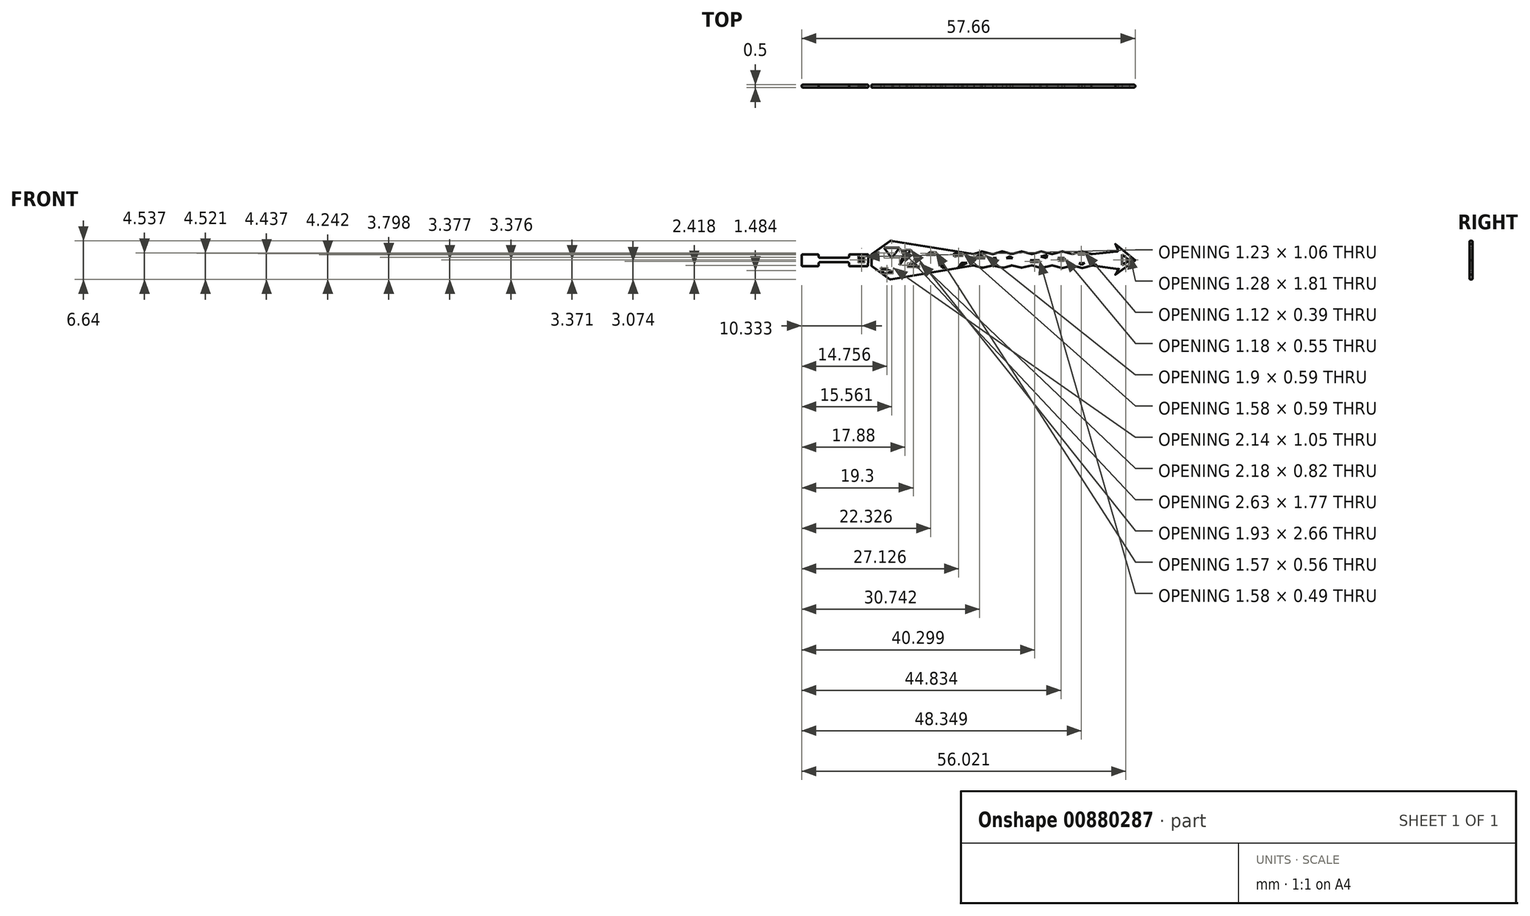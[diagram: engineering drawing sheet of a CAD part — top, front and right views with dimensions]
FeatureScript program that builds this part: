
annotation { "Feature Type Name" : "Feature", "Feature Type Description" : "" }
export const myFeature = defineFeature(function(context is Context, id is Id, definition is map)
    precondition{}
    {
        {
            var Q0;
            Q0=qCreatedBy(makeId("Front.planeOp"),FACE);
            var sketch = newSketch(context, id + "F0", { "sketchPlane" : qUnion([Q0])});
            skLineSegment(sketch, "E0", {"start": v(14.04, 0) * mm, "end": v(10.62, 2.77) * mm});
            skLineSegment(sketch, "E1", {"start": v(10.62, 2.77) * mm, "end": v(11.16, 1.51) * mm});
            skLineSegment(sketch, "E2", {"start": v(11.16, 1.51) * mm, "end": v(6.56, 1.02) * mm});
            skLineSegment(sketch, "E3", {"start": v(6.56, 1.02) * mm, "end": v(4.86, 1.51) * mm});
            skLineSegment(sketch, "E4", {"start": v(4.86, 1.51) * mm, "end": v(3.19, 1.02) * mm});
            skLineSegment(sketch, "E5", {"start": v(3.19, 1.02) * mm, "end": v(1.45, 1.51) * mm});
            skLineSegment(sketch, "E6", {"start": v(1.45, 1.51) * mm, "end": v(-0.33, 1.02) * mm});
            skLineSegment(sketch, "E7", {"start": v(-0.33, 1.02) * mm, "end": v(-2.2, 1.51) * mm});
            skLineSegment(sketch, "E8", {"start": v(-2.2, 1.51) * mm, "end": v(-3.84, 1.02) * mm});
            skLineSegment(sketch, "E9", {"start": v(-3.84, 1.02) * mm, "end": v(-5.58, 1.51) * mm});
            skLineSegment(sketch, "E10", {"start": v(-5.58, 1.51) * mm, "end": v(-7.29, 1.02) * mm});
            skLineSegment(sketch, "E11", {"start": v(-7.29, 1.02) * mm, "end": v(-8.89, 1.51) * mm});
            skLineSegment(sketch, "E12", {"start": v(-8.89, 1.51) * mm, "end": v(-10.66, 1.02) * mm});
            skLineSegment(sketch, "E13", {"start": v(-10.66, 1.02) * mm, "end": v(-12.44, 1.51) * mm});
            skLineSegment(sketch, "E14", {"start": v(-12.44, 1.51) * mm, "end": v(-13.9, 1.02) * mm});
            skLineSegment(sketch, "E15", {"start": v(-13.9, 1.02) * mm, "end": v(-28.31, 3.32) * mm});
            skLineSegment(sketch, "E16", {"start": v(-28.31, 3.32) * mm, "end": v(-31.55, 1.02) * mm});
            skLineSegment(sketch, "E17", {"start": v(-31.55, 1.02) * mm, "end": v(-31.55, -1) * mm});
            skLineSegment(sketch, "E18", {"start": v(-31.55, -1) * mm, "end": v(-28.31, -3.33) * mm});
            skLineSegment(sketch, "E19", {"start": v(-28.31, -3.33) * mm, "end": v(-13.9, -0.92) * mm});
            skLineSegment(sketch, "E20", {"start": v(-13.9, -0.92) * mm, "end": v(-12.44, -1.33) * mm});
            skLineSegment(sketch, "E21", {"start": v(-12.44, -1.33) * mm, "end": v(-10.66, -0.92) * mm});
            skLineSegment(sketch, "E22", {"start": v(-10.66, -0.92) * mm, "end": v(-8.89, -1.33) * mm});
            skLineSegment(sketch, "E23", {"start": v(-8.89, -1.33) * mm, "end": v(-7.29, -0.92) * mm});
            skLineSegment(sketch, "E24", {"start": v(-7.29, -0.92) * mm, "end": v(-5.58, -1.33) * mm});
            skLineSegment(sketch, "E25", {"start": v(-5.58, -1.33) * mm, "end": v(-3.84, -0.92) * mm});
            skLineSegment(sketch, "E26", {"start": v(-3.84, -0.92) * mm, "end": v(-2.2, -1.35) * mm});
            skLineSegment(sketch, "E27", {"start": v(-2.2, -1.35) * mm, "end": v(-0.33, -0.92) * mm});
            skLineSegment(sketch, "E28", {"start": v(-0.33, -0.92) * mm, "end": v(1.45, -1.35) * mm});
            skLineSegment(sketch, "E29", {"start": v(1.45, -1.35) * mm, "end": v(3.19, -0.92) * mm});
            skLineSegment(sketch, "E30", {"start": v(3.19, -0.92) * mm, "end": v(4.86, -1.35) * mm});
            skLineSegment(sketch, "E31", {"start": v(4.86, -1.35) * mm, "end": v(6.56, -0.92) * mm});
            skLineSegment(sketch, "E32", {"start": v(6.56, -0.92) * mm, "end": v(11.16, -1.53) * mm});
            skLineSegment(sketch, "E33", {"start": v(11.16, -1.53) * mm, "end": v(10.62, -2.51) * mm});
            skLineSegment(sketch, "E34", {"start": v(10.62, -2.51) * mm, "end": v(14.04, 0) * mm});
            skSolve(sketch);
        }
        {
            var Q0;
            Q0 = qSketchRegion(id + "F0", true);
            extrude(context, id + "F1", {"entities" : qUnion([Q0]), "depth" : .25 * mm, "offsetDistance" : 25 * mm, "hasSecondDirection" : true, "secondDirectionOppositeDirection" : true, "secondDirectionDepth" : .25 * mm});
        }
        {
            var Q0;
            Q0=qCreatedBy(makeId("Front.planeOp"),FACE);
            var sketch = newSketch(context, id + "F2", { "sketchPlane" : qUnion([Q0])});
            skLineSegment(sketch, "E35", {"start": v(13.04, 0) * mm, "end": v(11.76, 0.95) * mm});
            skLineSegment(sketch, "E36", {"start": v(11.76, 0.95) * mm, "end": v(11.76, -0.85) * mm});
            skLineSegment(sketch, "E37", {"start": v(11.76, -0.85) * mm, "end": v(13.04, 0) * mm});
            skLineSegment(sketch, "E38", {"start": v(5.29, -0.5) * mm, "end": v(4.76, -0.85) * mm});
            skLineSegment(sketch, "E39", {"start": v(4.76, -0.85) * mm, "end": v(4.36, -0.55) * mm});
            skLineSegment(sketch, "E40", {"start": v(4.36, -0.55) * mm, "end": v(5.29, -0.5) * mm});
            skLineSegment(sketch, "E41", {"start": v(5.29, 0.92) * mm, "end": v(4.76, 1.31) * mm});
            skLineSegment(sketch, "E42", {"start": v(4.76, 1.31) * mm, "end": v(4.17, 0.95) * mm});
            skLineSegment(sketch, "E43", {"start": v(4.17, 0.95) * mm, "end": v(5.29, 0.92) * mm});
            skLineSegment(sketch, "E44", {"start": v(1.8, 0.33) * mm, "end": v(0.62, 0.33) * mm});
            skLineSegment(sketch, "E45", {"start": v(0.62, 0.33) * mm, "end": v(1.36, -0.22) * mm});
            skLineSegment(sketch, "E46", {"start": v(1.36, -0.22) * mm, "end": v(1.8, 0.33) * mm});
            skLineSegment(sketch, "E47", {"start": v(-1.18, 0.92) * mm, "end": v(-2.27, 0.6) * mm});
            skLineSegment(sketch, "E48", {"start": v(-2.27, 0.6) * mm, "end": v(-1.35, 0.33) * mm});
            skLineSegment(sketch, "E49", {"start": v(-1.35, 0.33) * mm, "end": v(-1.18, 0.92) * mm});
            skLineSegment(sketch, "E50", {"start": v(-2.53, 0) * mm, "end": v(-3.45, -0.5) * mm});
            skLineSegment(sketch, "E51", {"start": v(-3.45, -0.5) * mm, "end": v(-4.11, 0) * mm});
            skLineSegment(sketch, "E52", {"start": v(-4.11, 0) * mm, "end": v(-2.53, 0) * mm});
            skLineSegment(sketch, "E53", {"start": v(-8.25, 0.33) * mm, "end": v(-7.63, 0.66) * mm});
            skLineSegment(sketch, "E54", {"start": v(-7.63, 0.66) * mm, "end": v(-7.18, 0.33) * mm});
            skLineSegment(sketch, "E55", {"start": v(-7.18, 0.33) * mm, "end": v(-8.25, 0.33) * mm});
            skLineSegment(sketch, "E56", {"start": v(-10.55, -0.5) * mm, "end": v(-9.94, 0.33) * mm});
            skLineSegment(sketch, "E57", {"start": v(-9.94, 0.33) * mm, "end": v(-10.51, 0.33) * mm});
            skLineSegment(sketch, "E58", {"start": v(-10.51, 0.33) * mm, "end": v(-10.55, -0.5) * mm});
            skLineSegment(sketch, "E59", {"start": v(-11.93, 0.33) * mm, "end": v(-12.72, 0.92) * mm});
            skLineSegment(sketch, "E60", {"start": v(-12.72, 0.92) * mm, "end": v(-13.83, 0.33) * mm});
            skLineSegment(sketch, "E61", {"start": v(-13.83, 0.33) * mm, "end": v(-11.93, 0.33) * mm});
            skLineSegment(sketch, "E62", {"start": v(-15.05, -0.5) * mm, "end": v(-16.63, -1.33) * mm});
            skLineSegment(sketch, "E63", {"start": v(-16.63, -1.33) * mm, "end": v(-16, -0.5) * mm});
            skLineSegment(sketch, "E64", {"start": v(-16, -0.5) * mm, "end": v(-15.05, -0.5) * mm});
            skLineSegment(sketch, "E65", {"start": v(-17.28, 0.63) * mm, "end": v(-15.7, 0.92) * mm});
            skLineSegment(sketch, "E66", {"start": v(-15.7, 0.92) * mm, "end": v(-17.28, 1.22) * mm});
            skLineSegment(sketch, "E67", {"start": v(-17.28, 1.22) * mm, "end": v(-17.28, 0.63) * mm});
            skLineSegment(sketch, "E68", {"start": v(-18.8, -1.31) * mm, "end": v(-19.68, -0.65) * mm});
            skLineSegment(sketch, "E69", {"start": v(-19.68, -0.65) * mm, "end": v(-19.33, -1.31) * mm});
            skLineSegment(sketch, "E70", {"start": v(-19.33, -1.31) * mm, "end": v(-18.8, -1.31) * mm});
            skLineSegment(sketch, "E71", {"start": v(-21.26, 1.48) * mm, "end": v(-20.5, 0.92) * mm});
            skLineSegment(sketch, "E72", {"start": v(-20.5, 0.92) * mm, "end": v(-22.08, 0.92) * mm});
            skLineSegment(sketch, "E73", {"start": v(-22.08, 0.92) * mm, "end": v(-21.26, 1.48) * mm});
            skLineSegment(sketch, "E74", {"start": v(-23.23, -1.31) * mm, "end": v(-24.33, -0.5) * mm});
            skLineSegment(sketch, "E75", {"start": v(-24.33, -0.5) * mm, "end": v(-25.41, -1.07) * mm});
            skLineSegment(sketch, "E76", {"start": v(-25.41, -1.07) * mm, "end": v(-23.23, -1.31) * mm});
            skLineSegment(sketch, "E77", {"start": v(-29.37, 2.1) * mm, "end": v(-26.74, 2.1) * mm});
            skLineSegment(sketch, "E78", {"start": v(-26.74, 2.1) * mm, "end": v(-28.07, 0.33) * mm});
            skLineSegment(sketch, "E79", {"start": v(-28.07, 0.33) * mm, "end": v(-29.37, 2.1) * mm});
            skLineSegment(sketch, "E80", {"start": v(-24.77, 1.74) * mm, "end": v(-26.7, -0.85) * mm});
            skLineSegment(sketch, "E81", {"start": v(-26.7, -0.85) * mm, "end": v(-25.56, 1.8) * mm});
            skLineSegment(sketch, "E82", {"start": v(-25.56, 1.8) * mm, "end": v(-24.77, 1.74) * mm});
            skLineSegment(sketch, "E83", {"start": v(-27.8, -1.97) * mm, "end": v(-29.93, -1.31) * mm});
            skLineSegment(sketch, "E84", {"start": v(-29.93, -1.31) * mm, "end": v(-29.37, -2.36) * mm});
            skLineSegment(sketch, "E85", {"start": v(-29.37, -2.36) * mm, "end": v(-27.8, -1.97) * mm});
            skSolve(sketch);
        }
        {
            var Q0;
            Q0 = qSketchRegion(id + "F2", true);
            extrude(context, id + "F3", {"entities" : qUnion([Q0]), "operationType" : NewBodyOperationType.REMOVE, "oppositeDirection" : true, "depth" : 25 * mm, "offsetDistance" : 25 * mm, "hasSecondDirection" : true, "secondDirectionOppositeDirection" : false, "secondDirectionDepth" : 25 * mm});
        }
        {
            var Q0;
            Q0=makeQuery(id+"F1.opExtrude","CAP_EDGE",EDGE,{"disambiguationData":[OSD([sQuery(id+"F0.wireOp",EDGE,"E0")])],"isStart":true});
            var Q1;
            Q1=makeQuery(id+"F1.opExtrude","CAP_EDGE",EDGE,{"disambiguationData":[OSD([sQuery(id+"F0.wireOp",EDGE,"E0")])],"isStart":false});
            var Q2;
            Q2=makeQuery(id+"F1.opExtrude","CAP_EDGE",EDGE,{"disambiguationData":[OSD([sQuery(id+"F0.wireOp",EDGE,"E34")])],"isStart":true});
            var Q3;
            Q3=makeQuery(id+"F1.opExtrude","CAP_EDGE",EDGE,{"disambiguationData":[OSD([sQuery(id+"F0.wireOp",EDGE,"E34")])],"isStart":false});
            fillet(context, id + "F4", {"entities" : qUnion([Q0, Q1, Q2, Q3]), "radius" : .2 * mm, "tangentPropagation" : true, "allowEdgeOverflow" : false});
        }
        {
            var Q0;
            Q0=makeQuery(id+"F1.opExtrude","SWEPT_FACE",FACE,{"disambiguationData":[OSD([sQuery(id+"F0.wireOp",EDGE,"E2")])]});
            fillet(context, id + "F5", {"entities" : qUnion([Q0]), "radius" : .2 * mm, "tangentPropagation" : true, "allowEdgeOverflow" : false});
        }
        {
            var Q0;
            Q0=makeQuery(id+"F1.opExtrude","CAP_EDGE",EDGE,{"disambiguationData":[OSD([sQuery(id+"F0.wireOp",EDGE,"E32")])],"isStart":true});
            var Q1;
            Q1=makeQuery(id+"F1.opExtrude","CAP_EDGE",EDGE,{"disambiguationData":[OSD([sQuery(id+"F0.wireOp",EDGE,"E32")])],"isStart":false});
            fillet(context, id + "F6", {"entities" : qUnion([Q0, Q1]), "radius" : .2 * mm, "tangentPropagation" : true, "allowEdgeOverflow" : false});
        }
        {
            var Q0;
            Q0=makeQuery(id+"F1.opExtrude","CAP_EDGE",EDGE,{"disambiguationData":[OSD([sQuery(id+"F0.wireOp",EDGE,"E31")])],"isStart":false});
            var Q1;
            Q1=makeQuery(id+"F1.opExtrude","CAP_EDGE",EDGE,{"disambiguationData":[OSD([sQuery(id+"F0.wireOp",EDGE,"E30")])],"isStart":false});
            var Q2;
            Q2=makeQuery(id+"F1.opExtrude","SWEPT_FACE",FACE,{"disambiguationData":[OSD([sQuery(id+"F0.wireOp",EDGE,"E31")])]});
            var Q3;
            Q3=makeQuery(id+"F1.opExtrude","SWEPT_FACE",FACE,{"disambiguationData":[OSD([sQuery(id+"F0.wireOp",EDGE,"E30")])]});
            var Q4;
            Q4=makeQuery(id+"F1.opExtrude","SWEPT_FACE",FACE,{"disambiguationData":[OSD([sQuery(id+"F0.wireOp",EDGE,"E29")])]});
            var Q5;
            Q5=makeQuery(id+"F1.opExtrude","SWEPT_FACE",FACE,{"disambiguationData":[OSD([sQuery(id+"F0.wireOp",EDGE,"E28")])]});
            var Q6;
            Q6=makeQuery(id+"F1.opExtrude","SWEPT_FACE",FACE,{"disambiguationData":[OSD([sQuery(id+"F0.wireOp",EDGE,"E27")])]});
            var Q7;
            Q7=makeQuery(id+"F1.opExtrude","SWEPT_FACE",FACE,{"disambiguationData":[OSD([sQuery(id+"F0.wireOp",EDGE,"E26")])]});
            var Q8;
            Q8=makeQuery(id+"F1.opExtrude","SWEPT_FACE",FACE,{"disambiguationData":[OSD([sQuery(id+"F0.wireOp",EDGE,"E25")])]});
            var Q9;
            Q9=makeQuery(id+"F1.opExtrude","SWEPT_FACE",FACE,{"disambiguationData":[OSD([sQuery(id+"F0.wireOp",EDGE,"E24")])]});
            var Q10;
            Q10=makeQuery(id+"F1.opExtrude","SWEPT_FACE",FACE,{"disambiguationData":[OSD([sQuery(id+"F0.wireOp",EDGE,"E22")])]});
            var Q11;
            Q11=makeQuery(id+"F1.opExtrude","CAP_EDGE",EDGE,{"disambiguationData":[OSD([sQuery(id+"F0.wireOp",EDGE,"E20")])],"isStart":true});
            var Q12;
            Q12=makeQuery(id+"F1.opExtrude","SWEPT_FACE",FACE,{"disambiguationData":[OSD([sQuery(id+"F0.wireOp",EDGE,"E19")])]});
            var Q13;
            Q13=makeQuery(id+"F1.opExtrude","SWEPT_FACE",FACE,{"disambiguationData":[OSD([sQuery(id+"F0.wireOp",EDGE,"E20")])]});
            var Q14;
            Q14=makeQuery(id+"F1.opExtrude","SWEPT_FACE",FACE,{"disambiguationData":[OSD([sQuery(id+"F0.wireOp",EDGE,"E18")])]});
            var Q15;
            Q15=makeQuery(id+"F1.opExtrude","SWEPT_FACE",FACE,{"disambiguationData":[OSD([sQuery(id+"F0.wireOp",EDGE,"E17")])]});
            var Q16;
            Q16=makeQuery(id+"F1.opExtrude","SWEPT_FACE",FACE,{"disambiguationData":[OSD([sQuery(id+"F0.wireOp",EDGE,"E16")])]});
            var Q17;
            Q17=makeQuery(id+"F1.opExtrude","SWEPT_FACE",FACE,{"disambiguationData":[OSD([sQuery(id+"F0.wireOp",EDGE,"E15")])]});
            var Q18;
            Q18=makeQuery(id+"F1.opExtrude","SWEPT_FACE",FACE,{"disambiguationData":[OSD([sQuery(id+"F0.wireOp",EDGE,"E13")])]});
            var Q19;
            Q19=makeQuery(id+"F1.opExtrude","CAP_EDGE",EDGE,{"disambiguationData":[OSD([sQuery(id+"F0.wireOp",EDGE,"E11")])],"isStart":true});
            var Q20;
            Q20=makeQuery(id+"F1.opExtrude","SWEPT_FACE",FACE,{"disambiguationData":[OSD([sQuery(id+"F0.wireOp",EDGE,"E11")])]});
            var Q21;
            Q21=makeQuery(id+"F1.opExtrude","SWEPT_FACE",FACE,{"disambiguationData":[OSD([sQuery(id+"F0.wireOp",EDGE,"E10")])]});
            var Q22;
            Q22=makeQuery(id+"F1.opExtrude","SWEPT_FACE",FACE,{"disambiguationData":[OSD([sQuery(id+"F0.wireOp",EDGE,"E9")])]});
            var Q23;
            Q23=makeQuery(id+"F1.opExtrude","SWEPT_FACE",FACE,{"disambiguationData":[OSD([sQuery(id+"F0.wireOp",EDGE,"E8")])]});
            var Q24;
            Q24=makeQuery(id+"F1.opExtrude","SWEPT_FACE",FACE,{"disambiguationData":[OSD([sQuery(id+"F0.wireOp",EDGE,"E7")])]});
            var Q25;
            Q25=makeQuery(id+"F1.opExtrude","SWEPT_FACE",FACE,{"disambiguationData":[OSD([sQuery(id+"F0.wireOp",EDGE,"E6")])]});
            var Q26;
            Q26=makeQuery(id+"F1.opExtrude","SWEPT_FACE",FACE,{"disambiguationData":[OSD([sQuery(id+"F0.wireOp",EDGE,"E5")])]});
            var Q27;
            Q27=makeQuery(id+"F1.opExtrude","SWEPT_FACE",FACE,{"disambiguationData":[OSD([sQuery(id+"F0.wireOp",EDGE,"E4")])]});
            fillet(context, id + "F7", {"entities" : qUnion([Q0, Q1, Q2, Q3, Q4, Q5, Q6, Q7, Q8, Q9, Q10, Q11, Q12, Q13, Q14, Q15, Q16, Q17, Q18, Q19, Q20, Q21, Q22, Q23, Q24, Q25, Q26, Q27]), "radius" : .1 * mm, "tangentPropagation" : true, "allowEdgeOverflow" : false});
        }
        {
            var Q0;
            Q0=qCreatedBy(makeId("Front.planeOp"),FACE);
            var sketch = newSketch(context, id + "F8", { "sketchPlane" : qUnion([Q0])});
            skLineSegment(sketch, "E86", {"start": v(-32.06, 1.01) * mm, "end": v(-43.62, 1.01) * mm});
            skLineSegment(sketch, "E87", {"start": v(-43.62, 1.01) * mm, "end": v(-43.62, -1.08) * mm});
            skLineSegment(sketch, "E88", {"start": v(-43.62, -1.08) * mm, "end": v(-32.2, -1.08) * mm});
            skLineSegment(sketch, "E89", {"start": v(-32.2, -1.08) * mm, "end": v(-32.06, 1.01) * mm});
            skSolve(sketch);
        }
        {
            var Q0;
            Q0 = qSketchRegion(id + "F8", true);
            extrude(context, id + "F9", {"entities" : qUnion([Q0]), "depth" : .25 * mm, "offsetDistance" : 25 * mm, "hasSecondDirection" : true, "secondDirectionOppositeDirection" : true, "secondDirectionDepth" : .25 * mm});
        }
        {
            var Q0;
            Q0=qCreatedBy(makeId("Front.planeOp"),FACE);
            var sketch = newSketch(context, id + "F10", { "sketchPlane" : qUnion([Q0])});
            skLineSegment(sketch, "E90", {"start": v(-33.25, 0.17) * mm, "end": v(-33.76, 0.59) * mm});
            skLineSegment(sketch, "E91", {"start": v(-33.76, 0.59) * mm, "end": v(-33.9, 0.41) * mm});
            skLineSegment(sketch, "E92", {"start": v(-33.9, 0.41) * mm, "end": v(-33.57, 0.14) * mm});
            skLineSegment(sketch, "E93", {"start": v(-33.57, 0.14) * mm, "end": v(-33.9, -0.13) * mm});
            skLineSegment(sketch, "E94", {"start": v(-33.9, -0.13) * mm, "end": v(-33.72, -0.36) * mm});
            skLineSegment(sketch, "E95", {"start": v(-33.72, -0.36) * mm, "end": v(-33.39, -0.1) * mm});
            skLineSegment(sketch, "E96", {"start": v(-33.39, -0.1) * mm, "end": v(-33.1, -0.48) * mm});
            skLineSegment(sketch, "E97", {"start": v(-33.1, -0.48) * mm, "end": v(-32.82, -0.26) * mm});
            skLineSegment(sketch, "E98", {"start": v(-32.82, -0.26) * mm, "end": v(-33.02, 0) * mm});
            skLineSegment(sketch, "E99", {"start": v(-33.02, 0) * mm, "end": v(-32.67, 0.28) * mm});
            skLineSegment(sketch, "E100", {"start": v(-32.67, 0.28) * mm, "end": v(-32.98, 0.41) * mm});
            skLineSegment(sketch, "E101", {"start": v(-32.98, 0.41) * mm, "end": v(-33.25, 0.17) * mm});
            skLineSegment(sketch, "E102", {"start": v(-34.75, -0.35) * mm, "end": v(-34.85, -0.48) * mm});
            skLineSegment(sketch, "E103", {"start": v(-34.85, -0.48) * mm, "end": v(-35.07, -0.3) * mm});
            skLineSegment(sketch, "E104", {"start": v(-35.07, -0.3) * mm, "end": v(-34.91, -0.11) * mm});
            skLineSegment(sketch, "E105", {"start": v(-34.91, -0.11) * mm, "end": v(-35.13, 0.17) * mm});
            skLineSegment(sketch, "E106", {"start": v(-35.13, 0.17) * mm, "end": v(-34.83, 0.41) * mm});
            skLineSegment(sketch, "E107", {"start": v(-34.83, 0.41) * mm, "end": v(-34.64, 0.17) * mm});
            skLineSegment(sketch, "E108", {"start": v(-34.64, 0.17) * mm, "end": v(-34.33, 0.41) * mm});
            skLineSegment(sketch, "E109", {"start": v(-34.33, 0.41) * mm, "end": v(-34.06, 0.07) * mm});
            skLineSegment(sketch, "E110", {"start": v(-34.06, 0.07) * mm, "end": v(-34.46, -0.24) * mm});
            skLineSegment(sketch, "E111", {"start": v(-34.46, -0.24) * mm, "end": v(-34.14, -0.65) * mm});
            skLineSegment(sketch, "E112", {"start": v(-34.14, -0.65) * mm, "end": v(-34.44, -0.65) * mm});
            skLineSegment(sketch, "E113", {"start": v(-34.44, -0.65) * mm, "end": v(-34.75, -0.35) * mm});
            skLineSegment(sketch, "E114", {"start": v(-36, -0.11) * mm, "end": v(-36.36, 0.35) * mm});
            skLineSegment(sketch, "E115", {"start": v(-36.36, 0.35) * mm, "end": v(-36.67, 0.1) * mm});
            skLineSegment(sketch, "E116", {"start": v(-36.67, 0.1) * mm, "end": v(-36.5, -0.11) * mm});
            skLineSegment(sketch, "E117", {"start": v(-36.5, -0.11) * mm, "end": v(-36.97, -0.48) * mm});
            skLineSegment(sketch, "E118", {"start": v(-36.97, -0.48) * mm, "end": v(-36.67, -0.59) * mm});
            skLineSegment(sketch, "E119", {"start": v(-36.67, -0.59) * mm, "end": v(-36.28, -0.28) * mm});
            skLineSegment(sketch, "E120", {"start": v(-36.28, -0.28) * mm, "end": v(-36.24, -0.3) * mm});
            skLineSegment(sketch, "E121", {"start": v(-36.24, -0.3) * mm, "end": v(-36, -0.11) * mm});
            skLineSegment(sketch, "E122", {"start": v(-37.74, -0.39) * mm, "end": v(-38.05, 0.29) * mm});
            skLineSegment(sketch, "E123", {"start": v(-38.05, 0.29) * mm, "end": v(-38.54, 0.06) * mm});
            skLineSegment(sketch, "E124", {"start": v(-38.54, 0.06) * mm, "end": v(-38.54, -0.18) * mm});
            skLineSegment(sketch, "E125", {"start": v(-38.54, -0.18) * mm, "end": v(-38.32, -0.39) * mm});
            skLineSegment(sketch, "E126", {"start": v(-38.32, -0.39) * mm, "end": v(-37.88, -0.39) * mm});
            skLineSegment(sketch, "E127", {"start": v(-37.88, -0.39) * mm, "end": v(-37.74, -0.39) * mm});
            skLineSegment(sketch, "E128", {"start": v(-39.64, 0.52) * mm, "end": v(-40.27, 0) * mm});
            skLineSegment(sketch, "E129", {"start": v(-40.27, 0) * mm, "end": v(-39.7, -0.39) * mm});
            skLineSegment(sketch, "E130", {"start": v(-39.7, -0.39) * mm, "end": v(-39.64, 0.52) * mm});
            skLineSegment(sketch, "E131", {"start": v(-41.78, -0.39) * mm, "end": v(-43.1, -0.39) * mm});
            skLineSegment(sketch, "E132", {"start": v(-43.1, -0.39) * mm, "end": v(-43.1, 0.7) * mm});
            skLineSegment(sketch, "E133", {"start": v(-43.1, 0.7) * mm, "end": v(-41.78, -0.39) * mm});
            skSolve(sketch);
        }
        {
            var Q0;
            Q0=makeQuery(id+"F10.imprint","IMPRINT",FACE,{"disambiguationData":[TD([[makeQuery(id+"F10.imprint","IMPRINT",EDGE,{"derivedFrom":sQuery(id+"F10.wireOp",EDGE,"E90")}),1.0]])]});
            extrude(context, id + "F11", {"entities" : qUnion([Q0]), "operationType" : NewBodyOperationType.REMOVE, "oppositeDirection" : true, "depth" : 25 * mm, "offsetDistance" : 25 * mm, "hasSecondDirection" : true, "secondDirectionOppositeDirection" : false, "secondDirectionDepth" : 25 * mm});
        }
        {
            var Q0;
            Q0=makeQuery(id+"F9.opExtrude","SWEPT_FACE",FACE,{"disambiguationData":[OSD([sQuery(id+"F8.wireOp",EDGE,"E88")])]});
            var Q1;
            Q1=makeQuery(id+"F9.opExtrude","SWEPT_FACE",FACE,{"disambiguationData":[OSD([sQuery(id+"F8.wireOp",EDGE,"E86")])]});
            var Q2;
            Q2=makeQuery(id+"F9.opExtrude","SWEPT_FACE",FACE,{"disambiguationData":[OSD([sQuery(id+"F8.wireOp",EDGE,"E89")])]});
            var Q3;
            Q3=makeQuery(id+"F9.opExtrude","SWEPT_FACE",FACE,{"disambiguationData":[OSD([sQuery(id+"F8.wireOp",EDGE,"E87")])]});
            fillet(context, id + "F12", {"entities" : qUnion([Q0, Q1, Q2, Q3]), "radius" : .2 * mm, "allowEdgeOverflow" : false});
        }
        {
            var Q0;
            Q0=qCreatedBy(makeId("Front.planeOp"),FACE);
            var sketch = newSketch(context, id + "F13", { "sketchPlane" : qUnion([Q0])});
            skLineSegment(sketch, "E134.bottom", {"start": v(-40.69, 0.4) * mm, "end": v(-35.43, 0.4) * mm});
            skLineSegment(sketch, "E134.top", {"start": v(-40.69, 1.43) * mm, "end": v(-35.43, 1.43) * mm});
            skLineSegment(sketch, "E134.left", {"start": v(-40.69, 0.4) * mm, "end": v(-40.69, 1.43) * mm});
            skLineSegment(sketch, "E134.right", {"start": v(-35.43, 0.4) * mm, "end": v(-35.43, 1.43) * mm});
            skLineSegment(sketch, "E135.bottom", {"start": v(-40.69, -0.36) * mm, "end": v(-35.43, -0.36) * mm});
            skLineSegment(sketch, "E135.top", {"start": v(-40.69, -1.58) * mm, "end": v(-35.43, -1.58) * mm});
            skLineSegment(sketch, "E135.left", {"start": v(-40.69, -0.36) * mm, "end": v(-40.69, -1.58) * mm});
            skLineSegment(sketch, "E135.right", {"start": v(-35.43, -0.36) * mm, "end": v(-35.43, -1.58) * mm});
            skSolve(sketch);
        }
        {
            var Q0;
            Q0 = qSketchRegion(id + "F13", true);
            extrude(context, id + "F14", {"entities" : qUnion([Q0]), "operationType" : NewBodyOperationType.REMOVE, "oppositeDirection" : true, "depth" : 25 * mm, "offsetDistance" : 25 * mm, "hasSecondDirection" : true, "secondDirectionOppositeDirection" : false, "secondDirectionDepth" : 25 * mm});
        }
        {
            var Q0;
            Q0=makeQuery(id+"F14.boolean.opBoolean","COPY",FACE,{"derivedFrom":makeQuery(id+"F14.opExtrude","SWEPT_FACE",FACE,{"disambiguationData":[OSD([sQuery(id+"F13.wireOp",EDGE,"E135.left")])]})});
            var Q1;
            Q1=makeQuery(id+"F14.boolean.opBoolean","COPY",FACE,{"derivedFrom":makeQuery(id+"F14.opExtrude","SWEPT_FACE",FACE,{"disambiguationData":[OSD([sQuery(id+"F13.wireOp",EDGE,"E135.bottom")])]})});
            var Q2;
            Q2=makeQuery(id+"F14.boolean.opBoolean","COPY",FACE,{"derivedFrom":makeQuery(id+"F14.opExtrude","SWEPT_FACE",FACE,{"disambiguationData":[OSD([sQuery(id+"F13.wireOp",EDGE,"E135.right")])]})});
            var Q3;
            Q3=makeQuery(id+"F14.boolean.opBoolean","COPY",FACE,{"derivedFrom":makeQuery(id+"F14.opExtrude","SWEPT_FACE",FACE,{"disambiguationData":[OSD([sQuery(id+"F13.wireOp",EDGE,"E134.bottom")])]})});
            var Q4;
            Q4=makeQuery(id+"F14.boolean.opBoolean","COPY",FACE,{"derivedFrom":makeQuery(id+"F14.opExtrude","SWEPT_FACE",FACE,{"disambiguationData":[OSD([sQuery(id+"F13.wireOp",EDGE,"E134.left")])]})});
            var Q5;
            Q5=makeQuery(id+"F14.boolean.opBoolean","COPY",FACE,{"derivedFrom":makeQuery(id+"F14.opExtrude","SWEPT_FACE",FACE,{"disambiguationData":[OSD([sQuery(id+"F13.wireOp",EDGE,"E134.right")])]})});
            fillet(context, id + "F15", {"entities" : qUnion([Q0, Q1, Q2, Q3, Q4, Q5]), "radius" : .2 * mm, "tangentPropagation" : true, "allowEdgeOverflow" : false});
        }
    });
